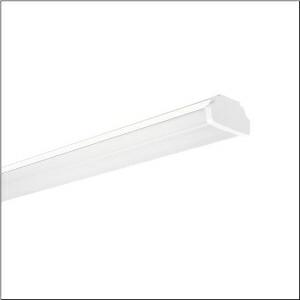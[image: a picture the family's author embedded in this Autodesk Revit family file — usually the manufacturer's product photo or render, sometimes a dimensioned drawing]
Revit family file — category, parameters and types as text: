
# Revit family: modario_r__31_ho_53bm812c1v4105_deab
name_source: partatom
category: Lighting Fixtures
units: mm (PartAtom-declared; Revit-internal decimal feet)

## family parameters
Cut with Voids When Loaded = No
Host = Face
Light Source = No
Part Type = Normal
Room Calculation Point = No
Round Connector Dimension = Use Diameter
Shared = No

## types (1)
- --- (1 x LED, 10520 lm, 63.8 W, 4000K)
    Apparent Load = 64 VA
    CIE Flux Codes = 47 80 95 92 100
    Color Rendering = 80
    Color Temperature = 4000K
    Default Elevation = 1800 mm
    Description = Modario® 31 HO, luminaire insert, of sheet steel, coil coated, white, length: 1.495mm, width: 81mm, height: 82mm, 5x system unit, system units: 299mm, LED rated luminous flux: 10.520lm, light colour: 840, control gear: ON/OFF Multilumen, CLOi, control gear: ECG Multilumen, with plug, 3-pole, with phase selection, mains connection: 220..240V, AC, 50/60Hz, start of lifetime: 64W, end of service life: 73W, through-wiring accessed according to module size, primary optical cover: cover, of PMMA, light emission: direct distribution, primary light characteristic: symmetric, protection rating (complete): IP20, protection rating (LED compartment): IP50, insulation class (complete): insulation class I (protective earthing), certification: CE, ENEC, VDE, UKCA, impact resistance: IK03, permissible ambient temperature for indoor applications: -35..+35°C, corresponds to IFS (International Featured Standards) requirements for safety and quality in the food industry, reducing of maximum allowable ambient temperature of 5°C with ceiling mounting, packaging unit: 1 piece
    Height = 92 mm
    Lamp = 1 x LED
    Lamp Light Flux = 10520 lm
    Lamp Power = 63.8 W
    Lamp count = 1
    Length = 1495 mm
    Luminous efficacy = 165 lm/W
    Manufacturer = Siteco
    ModVariant = No
    Model = 53BM812C1V4105
    Mounting Place = Ceiling
    Mounting Type = Pendant
    Number of Poles = 1
    OnlyDefault = Yes
    Power Factor = 1
    Product Name = Modario® 31 HO
    Product group = luminaire insert
    ProductGroupID = 902
    Protection Class = Protection class I
    Protection Degree = IP 20
    RLX_Detail_Level = 1
    RLX_Emergency_Light_Flux = 0 lm
    RLX_Emergency_Type = 0
    RLX_Emergency_Type_DB = No
    RlxData = <blob elided: 40021 chars, md5=f9847e62>
    Socket = socket
    Standby Power = 0 W
    System Light Flux = 10520 lm
    System Power = 64 W
    Type Comments = factory setting: luminous flux: 100 % | (A | C | E) | 144 mA
    Type Image = l_1341886.jpg
    URL = http://relux.com
    VarID = @adj_198484
    Voltage = 0 V
    Weight = 0.00 kg
    Width = 81 mm

## geometry (parser evidence)
native form markers: Blend x4, Sweep x13
no freeform markers — native parametric forms only
